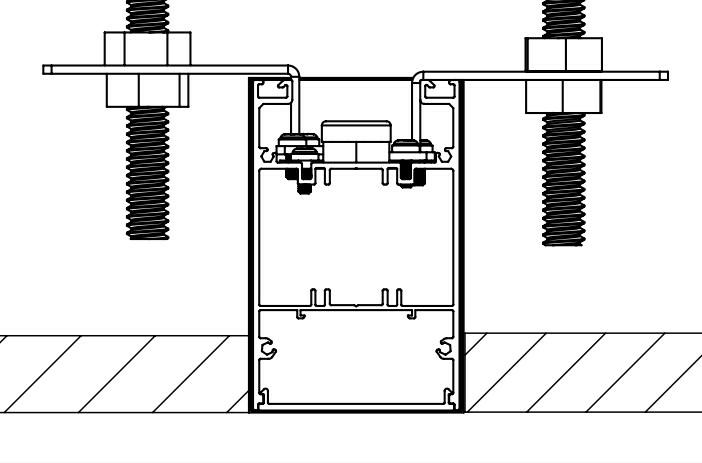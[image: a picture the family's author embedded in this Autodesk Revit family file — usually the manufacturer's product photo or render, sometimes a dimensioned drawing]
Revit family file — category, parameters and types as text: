
# Revit family: TECHOLED-IP2R-D_Series Led Light
name_source: partatom
category: Lighting Fixtures
units: mm (PartAtom-declared; Revit-internal decimal feet)

## family parameters
Cut with Voids When Loaded = No
Host = Face
Light Source = Yes
Part Type = Normal
Room Calculation Point = No
Round Connector Dimension = Use Diameter
Shared = No

## types (9) — shared parameters
Body Material = W-White
Color Filter = 16777215
Cord Length = 0' - 6"
Default Elevation = 4' - 0"
Description = IP-2R SERISE
Dimming Lamp Color Temperature Shift = <None>
Light Material = White
Light Source Height = 0' - 10 11/32"
Manufacturer = techoLED
Mounting Material = Stainless Steel
Tilt Angle = -90.00°

## per-type parameters (varying)
| type | Apparent Load | Length | Mounting Length | Photometric Web File | Wattage Comments |
| TECHOLED-IP2R-D-4-LO-30-U-W | 15 VA | 4' - 0" | 1' - 8" | generic | 15W |
| TECHOLED-IP2R-D-4-ME-30-U-W | 23 VA | 4' - 0" | 1' - 8" | TECHOLED-IP-D-4-ME-30.ies | 23W |
| TECHOLED-IP2R-D-4-HI-30-U-W | 31 VA | 4' - 0" | 1' - 8" | generic | 31W |
| TECHOLED-IP2R-D-6-LO-30-U-W | 23 VA | 6' - 0" | 2' - 8" | generic | 23W |
| TECHOLED-IP2R-D-6-ME-30-U-W | 34 VA | 4' - 0" | 1' - 8" | TECHOLED-IP-D-4-ME-30.ies | 34W |
| TECHOLED-IP2R-D-6-HI-30-U-W | 45 VA | 4' - 0" | 1' - 8" | generic | 45W |
| TECHOLED-IP2R-D-8-LO-30-U-W | 31 VA | 8' - 0" | 3' - 8" | generic | 31W |
| TECHOLED-IP2R-D-8-ME-30-U-W | 46 VA | 8' - 0" | 3' - 8" | TECHOLED-IP-D-4-ME-30.ies | 46W |
| TECHOLED-IP2R-D-8-HI-30-U-W | 61 VA | 8' - 0" | 3' - 8" | generic | 61W |

note: column(s) folded — value = type name in every type: Model

## geometry (parser evidence)
native form markers: Sweep x11
no freeform markers — native parametric forms only
